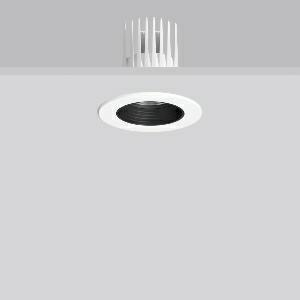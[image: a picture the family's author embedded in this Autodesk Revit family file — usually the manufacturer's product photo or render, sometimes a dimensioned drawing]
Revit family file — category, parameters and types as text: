
# Revit family: heledon_mini_e_901744_002_1_b3f1
name_source: partatom
category: Lighting Fixtures
units: mm (PartAtom-declared; Revit-internal decimal feet)

## family parameters
Cut with Voids When Loaded = No
Host = Face
Light Source = No
Part Type = Normal
Room Calculation Point = No
Round Connector Dimension = Use Diameter
Shared = No

## types (1)
- HELEDON mini E (1 x LED Modul 940, 2250 lm, 4000)
    Apparent Load = 20 VA
    Approval mark = CE
    CIE Flux Codes = 96 100 100 100 100
    Color Rendering = 92
    Color Temperature = 4000
    Default Elevation = 1800 mm
    Description = Series: HELEDON mini
Round recessed downlight. Housing: die-cast aluminium, powder-coated. Black plastic ring and recessed LED to prevent glare from the side. Optical assembly with lens made of plastic (polycarbonate) for the best homogeneous light distribution - can be changed without tools. Best colour rendering index Ra>90. Suitable for Recessed ceiling mounting. Installation without tools thanks to spring fastening system. Including separate LED converter with connecting cable 600 mm.High quality converter without flickering and stroboscopic effect. Through-wiring box (5 pole) available as accessory. The following accessories can be mounted without use of tools: interchangeable lenses, decorative glasses, honeycomb louvre, clear and frosted diffusers, white interchangeable plastic ring. 
Colour: traffic white, matt (RAL 9016)
Diameter: 124 mm
Height: 3 mm
Cut-out diameter: 114 mm
Recess height: 170 mm
Luminaire: recess height: 120 mm
Lamp: LED
Socket: without socket
Colour temperature: 4000K
Colour rendering index (CRI): 92
System power: 20 W
Rated luminous flux: 2250 lm
Luminous efficiency: 113 lm/W
Control gear: Regulated power supply
Protection class: II
Type of protection: IP 20
    Height = 0 mm  [stored 0 ft]
    Lamp = 1 x LED Modul 940
    Lamp Light Flux = 2250 lm
    Lamp count = 1
    Length = 124 mm  [stored 0.406824 ft]
    Lifetime = 50000 h
    Luminous efficacy = 113 lm/W
    Manufacturer = RZB
    ModVariant = No
    Model = 901744.002.1
    Mounting Place = Ceiling
    Mounting Type = Recessed
    Number of Poles = 1
    OnlyDefault = Yes
    Power Factor = 1
    Product Name = HELEDON mini E
    Product group = Recessed downlights
    ProductGroupID = 402
    Protection Class = Protection class II
    Protection Degree = IP 20
    RLX_Detail_Level = 1
    RLX_Emergency_Light_Flux = 0 lm
    RLX_Emergency_Type = 0
    RLX_Emergency_Type_DB = No
    RlxData = <blob elided: 125901 chars, md5=cd572db0>
    Socket = socket
    Standby Power = 0 W
    System Light Flux = 2250 lm
    System Power = 20 W
    Type Comments = Product without accessories
    Type Image = 901656.002.jpg
    URL = http://relux.com
    VarID = ---
    Voltage = 230 V
    Voltage Range = 220-240 V
    Weight = 0.00 kg
    Width = 0 mm  [stored 0 ft]

note: [stored X ft] marks values corroborated as IEEE doubles in the binary element streams (Revit-internal decimal feet)

## geometry (parser evidence)
native form markers: Blend x4, Sweep x10
no freeform markers — native parametric forms only
